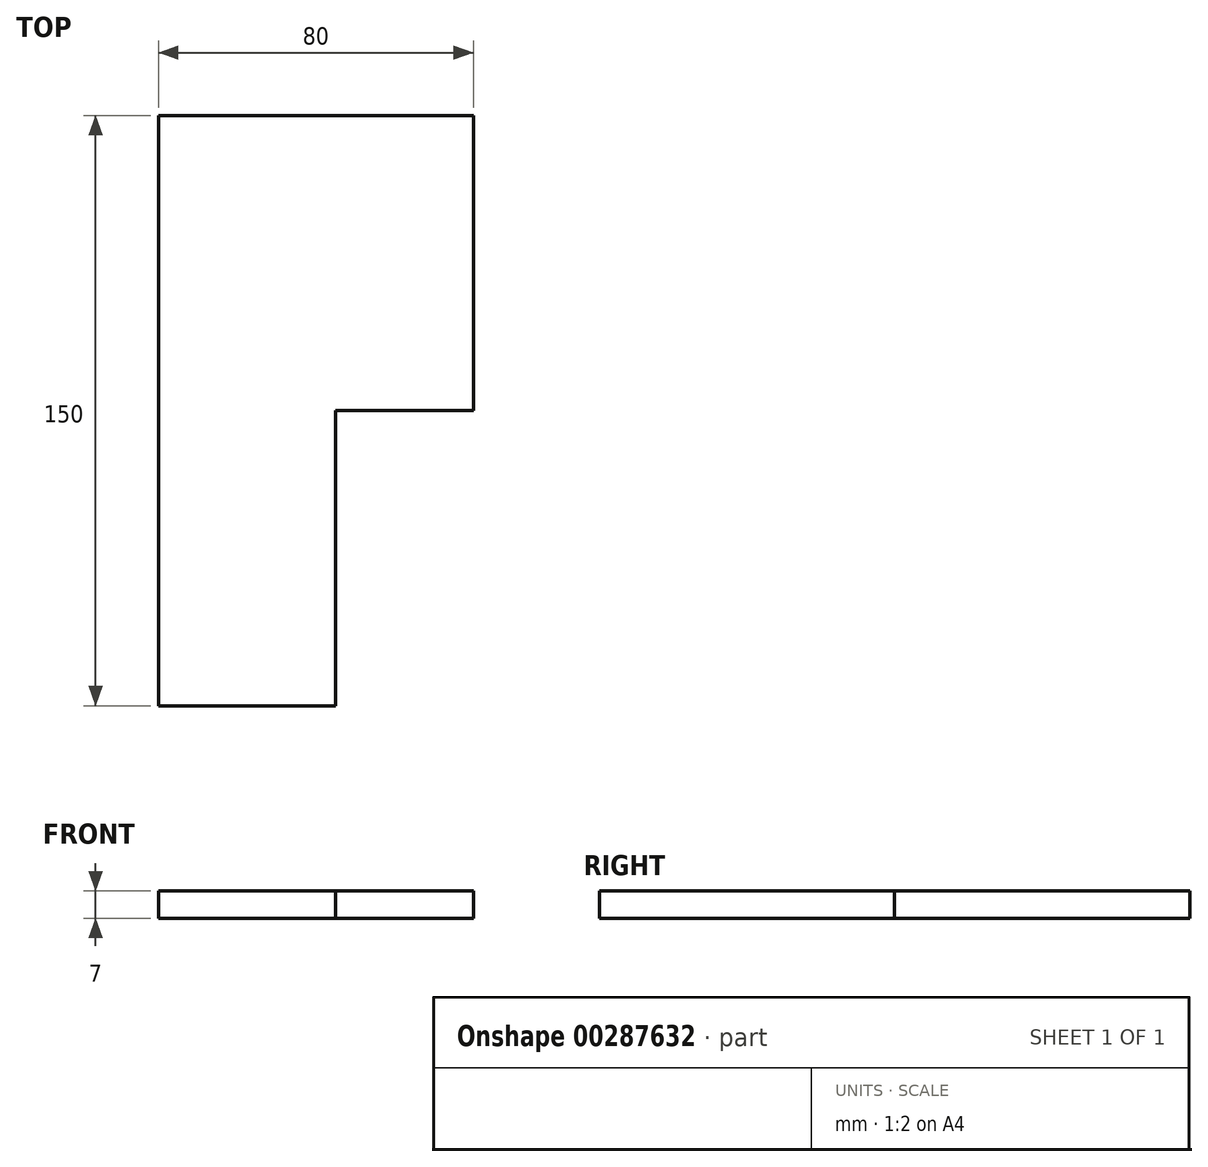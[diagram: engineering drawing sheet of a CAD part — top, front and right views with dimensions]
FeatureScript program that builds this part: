
annotation { "Feature Type Name" : "Feature", "Feature Type Description" : "" }
export const myFeature = defineFeature(function(context is Context, id is Id, definition is map)
    precondition{}
    {
        {
            var Q0;
            Q0=qCreatedBy(makeId("Top.planeOp"),FACE);
            var sketch = newSketch(context, id + "F0", { "sketchPlane" : qUnion([Q0])});
            skLineSegment(sketch, "E0", {"start": v(-19.82, -47.16) * mm, "end": v(-19.82, 102.84) * mm});
            skLineSegment(sketch, "E1", {"start": v(-19.82, 102.84) * mm, "end": v(60.18, 102.84) * mm});
            skLineSegment(sketch, "E2", {"start": v(60.18, 102.84) * mm, "end": v(60.18, 27.84) * mm});
            skLineSegment(sketch, "E3", {"start": v(60.18, 27.84) * mm, "end": v(25.18, 27.84) * mm});
            skLineSegment(sketch, "E4", {"start": v(-19.82, -47.16) * mm, "end": v(25.18, -47.16) * mm});
            skLineSegment(sketch, "E5", {"start": v(25.18, -47.16) * mm, "end": v(25.18, 27.84) * mm});
            skSolve(sketch);
        }
        {
            var Q0;
            Q0=qSketchRegion(id+"F0",true);
            extrude(context, id + "F1", {"entities" : qUnion([Q0]), "depth" : 7 * mm});
        }
    });
